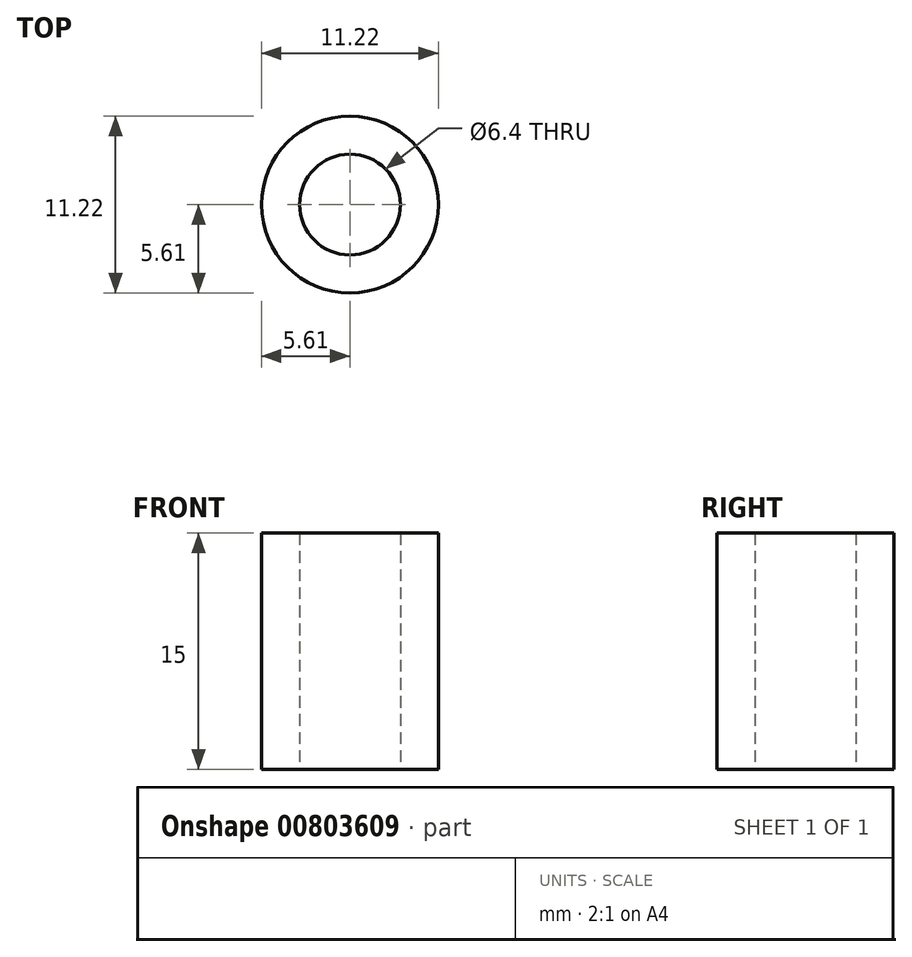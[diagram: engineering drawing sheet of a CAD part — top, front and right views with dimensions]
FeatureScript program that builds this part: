
annotation { "Feature Type Name" : "Feature", "Feature Type Description" : "" }
export const myFeature = defineFeature(function(context is Context, id is Id, definition is map)
    precondition{}
    {
        {
            var Q0;
            Q0=qCreatedBy(makeId("Top.planeOp"),FACE);
            var sketch = newSketch(context, id + "F0", { "sketchPlane" : qUnion([Q0])});
            skCircle(sketch, "E0", {"center": v(0, 0) * mm, "radius": 3.2 * mm});
            skCircle(sketch, "E1", {"center": v(0, 0) * mm, "radius": 5.61 * mm});
            skSolve(sketch);
        }
        {
            var Q0;
            Q0 = qSketchRegion(id + "F0", true);
            var Q1;
            {var subQ0=sQuery(id+"F0.wireOp",EDGE,"wiSwtj2A-BGhQ-P8X0-y9qm-9Bsc0NGXXVE2");Q1=makeQuery(id+"F0.imprint","IMPRINT",FACE,{"disambiguationData":[TD([[makeQuery(id+"F0.imprint","IMPRINT",EDGE,{"derivedFrom":subQ0}),1.0]])]});}
            extrude(context, id + "F1", {"entities" : qUnion([Q0, Q1]), "depth" : 15 * mm, "offsetDistance" : 25 * mm});
        }
    });
